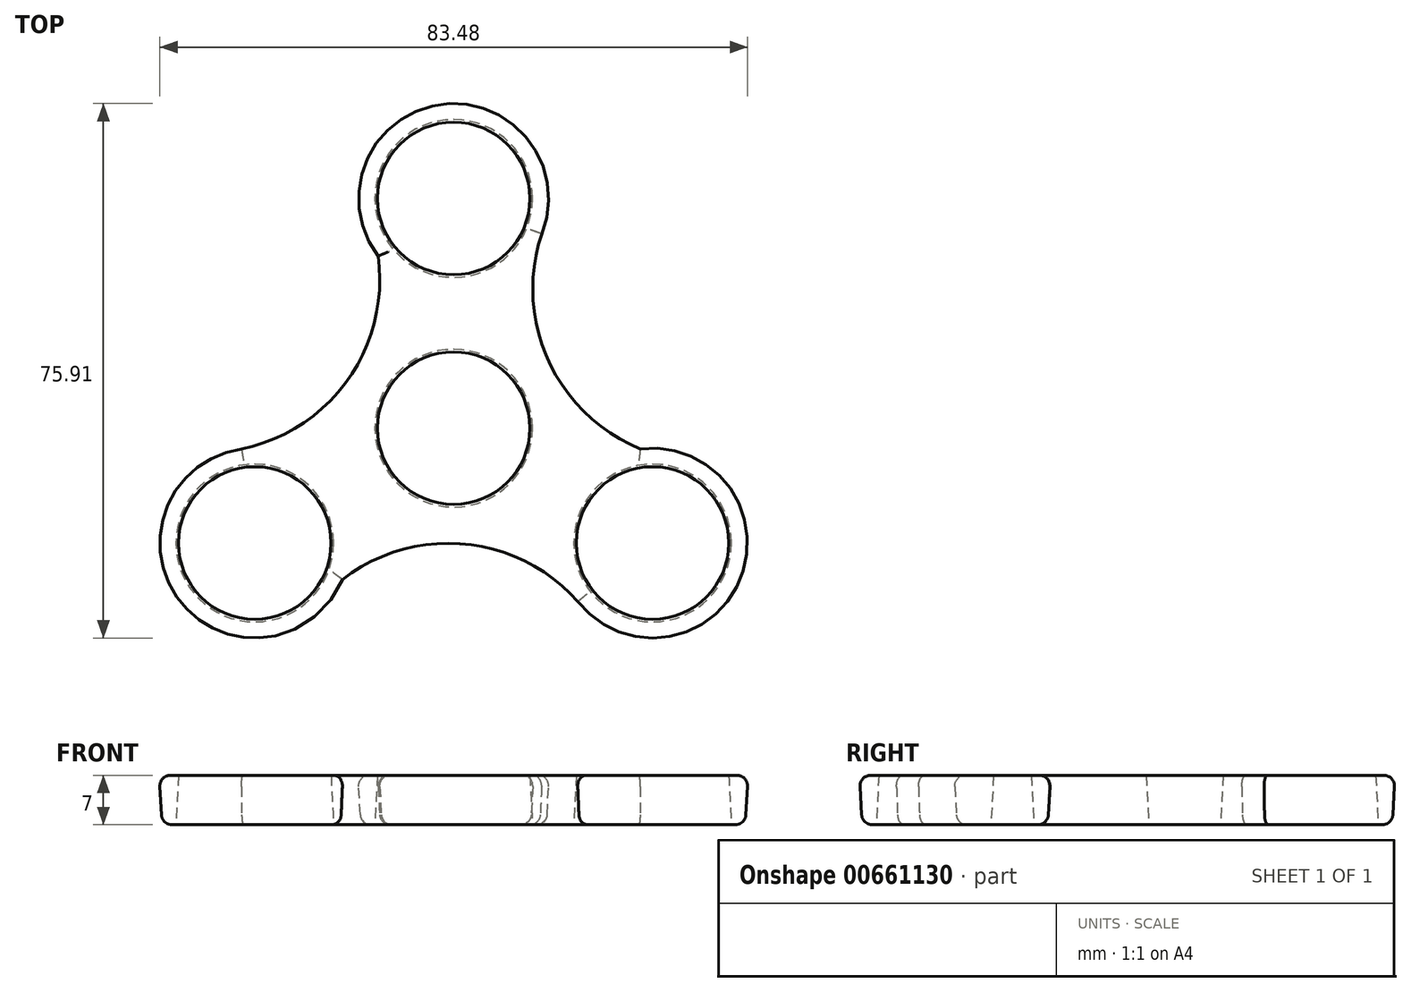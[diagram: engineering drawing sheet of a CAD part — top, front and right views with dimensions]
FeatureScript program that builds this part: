
annotation { "Feature Type Name" : "Feature", "Feature Type Description" : "" }
export const myFeature = defineFeature(function(context is Context, id is Id, definition is map)
    precondition{}
    {
        {
            var Q0;
            Q0=qCreatedBy(makeId("Top.planeOp"),FACE);
            var sketch = newSketch(context, id + "F0", { "sketchPlane" : qUnion([Q0])});
            skCircle(sketch, "E0", {"center": v(0, 0) * mm, "radius": 11.2 * mm});
            skCircle(sketch, "E1", {"center": v(0, 32.62) * mm, "radius": 11.2 * mm});
            skArc(sketch, "E2", {"start": v(12.24, 27.68) * mm, "mid": v(-1.8, 45.7) * mm, "end": v(-10.44, 24.55) * mm});
            skArc(sketch, "E3.1.0", {"start": v(-30.1, -3.24) * mm, "mid": v(-38.67, -24.41) * mm, "end": v(-16.04, -21.32) * mm});
            skCircle(sketch, "E3.1.1", {"center": v(-28.25, -16.31) * mm, "radius": 11.2 * mm});
            skArc(sketch, "E3.2.0", {"start": v(17.85, -24.44) * mm, "mid": v(40.48, -21.28) * mm, "end": v(26.48, -3.23) * mm});
            skCircle(sketch, "E3.2.1", {"center": v(28.25, -16.31) * mm, "radius": 11.2 * mm});
            skArc(sketch, "E4", {"start": v(12.24, 27.68) * mm, "mid": v(13.23, 9.4) * mm, "end": v(26.48, -3.23) * mm});
            skArc(sketch, "E5.1.0", {"start": v(-30.1, -3.24) * mm, "mid": v(-14.76, 6.76) * mm, "end": v(-10.44, 24.55) * mm});
            skArc(sketch, "E5.2.0", {"start": v(17.85, -24.44) * mm, "mid": v(1.53, -16.16) * mm, "end": v(-16.04, -21.32) * mm});
            skSolve(sketch);
        }
        {
            var Q0;
            Q0=makeQuery(id+"F0.imprint","IMPRINT",FACE,{"disambiguationData":[TD([[makeQuery(id+"F0.imprint","IMPRINT",EDGE,{"derivedFrom":sQuery(id+"F0.wireOp",EDGE,"E0")}),-1.0]])]});
            extrude(context, id + "F1", {"entities" : qUnion([Q0]), "depth" : 7 * mm, "offsetDistance" : 25 * mm, "hasDraft" : true, "draftAngle" : 3 * degree});
        }
        {
            var Q0;
            Q0=makeQuery(id+"F1.opExtrude","CAP_EDGE",EDGE,{"disambiguationData":[OSD([sQuery(id+"F0.wireOp",EDGE,"E3.2.0")])],"isStart":false});
            var Q1;
            Q1=makeQuery(id+"F1.opExtrude","CAP_EDGE",EDGE,{"disambiguationData":[OSD([sQuery(id+"F0.wireOp",EDGE,"E4")])],"isStart":false});
            var Q2;
            Q2=makeQuery(id+"F1.opExtrude","CAP_EDGE",EDGE,{"disambiguationData":[OSD([sQuery(id+"F0.wireOp",EDGE,"E2")])],"isStart":false});
            var Q3;
            Q3=makeQuery(id+"F1.opExtrude","CAP_EDGE",EDGE,{"disambiguationData":[OSD([sQuery(id+"F0.wireOp",EDGE,"E5.1.0")])],"isStart":false});
            var Q4;
            Q4=makeQuery(id+"F1.opExtrude","CAP_EDGE",EDGE,{"disambiguationData":[OSD([sQuery(id+"F0.wireOp",EDGE,"E3.1.0")])],"isStart":false});
            var Q5;
            Q5=makeQuery(id+"F1.opExtrude","CAP_EDGE",EDGE,{"disambiguationData":[OSD([sQuery(id+"F0.wireOp",EDGE,"E5.2.0")])],"isStart":false});
            fillet(context, id + "F2", {"entities" : qUnion([Q0, Q1, Q2, Q3, Q4, Q5]), "radius" : 1.5 * mm, "tangentPropagation" : true, "allowEdgeOverflow" : false});
        }
        {
            var Q0;
            Q0=makeQuery(id+"F1.opExtrude","CAP_EDGE",EDGE,{"disambiguationData":[OSD([sQuery(id+"F0.wireOp",EDGE,"E3.2.0")])],"isStart":true});
            var Q1;
            Q1=makeQuery(id+"F1.opExtrude","CAP_EDGE",EDGE,{"disambiguationData":[OSD([sQuery(id+"F0.wireOp",EDGE,"E4")])],"isStart":true});
            var Q2;
            Q2=makeQuery(id+"F1.opExtrude","CAP_EDGE",EDGE,{"disambiguationData":[OSD([sQuery(id+"F0.wireOp",EDGE,"E2")])],"isStart":true});
            var Q3;
            Q3=makeQuery(id+"F1.opExtrude","CAP_EDGE",EDGE,{"disambiguationData":[OSD([sQuery(id+"F0.wireOp",EDGE,"E5.1.0")])],"isStart":true});
            var Q4;
            Q4=makeQuery(id+"F1.opExtrude","CAP_EDGE",EDGE,{"disambiguationData":[OSD([sQuery(id+"F0.wireOp",EDGE,"E3.1.0")])],"isStart":true});
            var Q5;
            Q5=makeQuery(id+"F1.opExtrude","CAP_EDGE",EDGE,{"disambiguationData":[OSD([sQuery(id+"F0.wireOp",EDGE,"E5.2.0")])],"isStart":true});
            fillet(context, id + "F3", {"entities" : qUnion([Q0, Q1, Q2, Q3, Q4, Q5]), "radius" : 1.5 * mm, "tangentPropagation" : true, "allowEdgeOverflow" : false});
        }
    });
